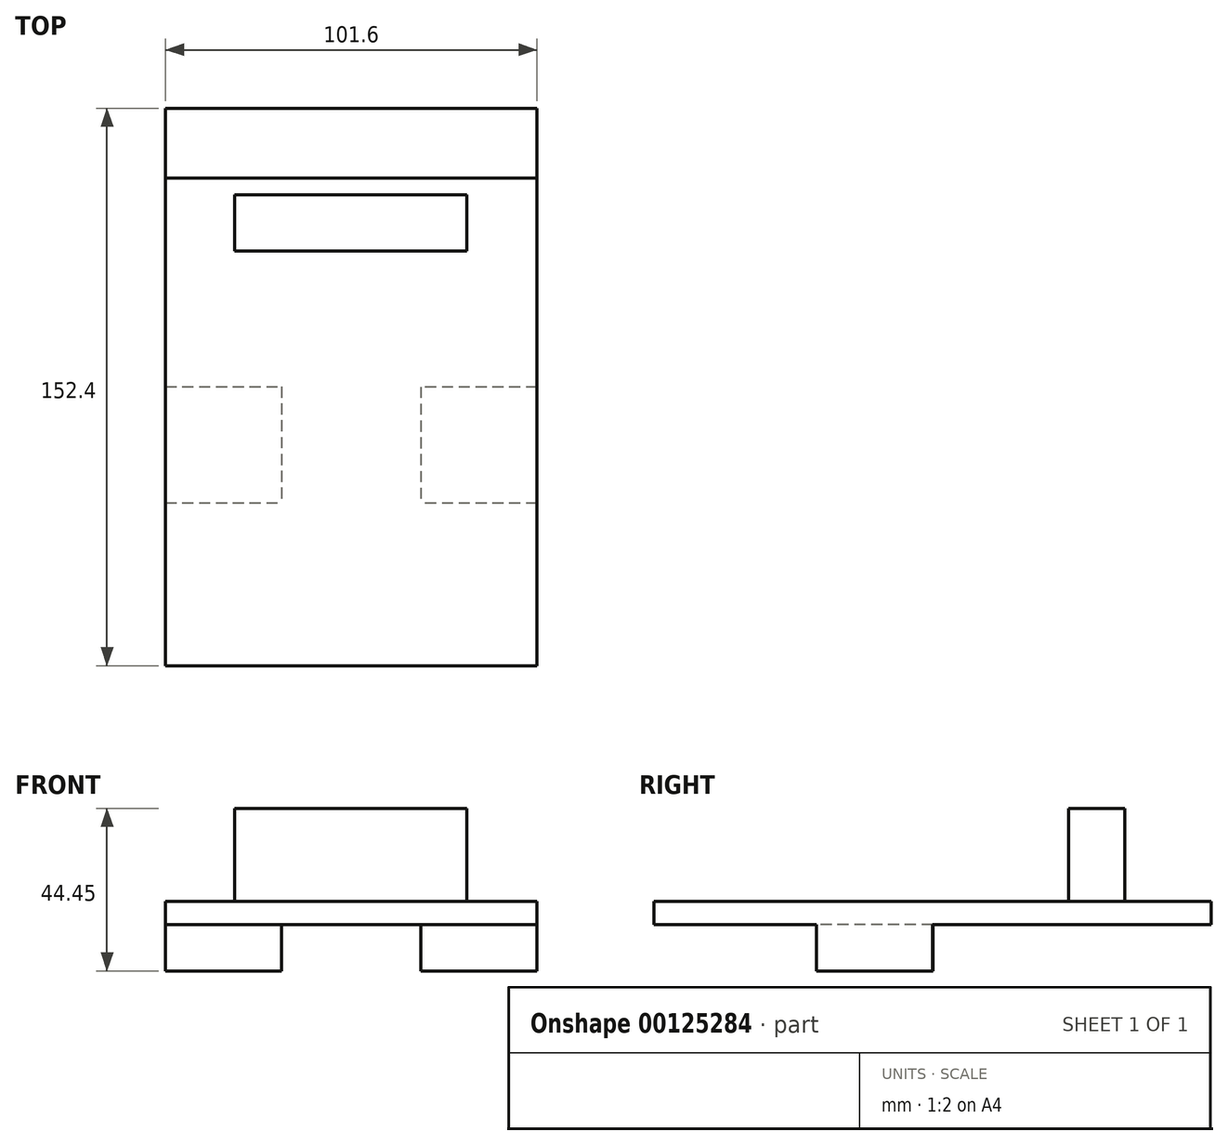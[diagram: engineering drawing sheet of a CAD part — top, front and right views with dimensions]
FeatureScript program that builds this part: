
annotation { "Feature Type Name" : "Feature", "Feature Type Description" : "" }
export const myFeature = defineFeature(function(context is Context, id is Id, definition is map)
    precondition{}
    {
        {
            var Q0;
            Q0=qCreatedBy(makeId("Top.planeOp"),FACE);
            var sketch = newSketch(context, id + "F0", { "sketchPlane" : qUnion([Q0])});
            skLineSegment(sketch, "E0.bottom", {"start": v(0, 0) * mm, "end": v(101.6, 0) * mm});
            skLineSegment(sketch, "E0.top", {"start": v(0, 152.4) * mm, "end": v(101.6, 152.4) * mm});
            skLineSegment(sketch, "E0.left", {"start": v(0, 0) * mm, "end": v(0, 152.4) * mm});
            skLineSegment(sketch, "E0.right", {"start": v(101.6, 0) * mm, "end": v(101.6, 152.4) * mm});
            skSolve(sketch);
        }
        {
            var Q0;
            Q0=makeQuery(id+"F0.imprint","IMPRINT",FACE,{"disambiguationData":[TD([[makeQuery(id+"F0.imprint","IMPRINT",EDGE,{"derivedFrom":sQuery(id+"F0.wireOp",EDGE,"E0.bottom")}),1.0]])]});
            extrude(context, id + "F1", {"entities" : qUnion([Q0]), "depth" : 6.35 * mm});
        }
        {
            var Q0;
            Q0=makeQuery(id+"F1.opExtrude","CAP_FACE",FACE,{"disambiguationData":[OSD([sQuery(id+"F0.wireOp",EDGE,"E0.bottom"),sQuery(id+"F0.wireOp",EDGE,"E0.top"),sQuery(id+"F0.wireOp",EDGE,"E0.left"),sQuery(id+"F0.wireOp",EDGE,"E0.right")])],"isStart":false});
            var sketch = newSketch(context, id + "F2", { "sketchPlane" : qUnion([Q0])});
            skLineSegment(sketch, "E1.bottom", {"start": v(18.86, 128.7) * mm, "end": v(82.36, 128.7) * mm});
            skLineSegment(sketch, "E1.top", {"start": v(18.86, 113.35) * mm, "end": v(82.36, 113.35) * mm});
            skLineSegment(sketch, "E1.left", {"start": v(18.86, 128.7) * mm, "end": v(18.86, 113.35) * mm});
            skLineSegment(sketch, "E1.right", {"start": v(82.36, 128.7) * mm, "end": v(82.36, 113.35) * mm});
            skSolve(sketch);
        }
        {
            var Q0;
            Q0=makeQuery(id+"F2.imprint","IMPRINT",FACE,{"disambiguationData":[TD([[makeQuery(id+"F2.imprint","IMPRINT",EDGE,{"derivedFrom":sQuery(id+"F2.wireOp",EDGE,"E1.bottom")}),-1.0]])]});
            extrude(context, id + "F3", {"entities" : qUnion([Q0]), "operationType" : NewBodyOperationType.ADD, "depth" : 25.4 * mm});
        }
        {
            var Q0;
            Q0=makeQuery(id+"F1.opExtrude","CAP_FACE",FACE,{"disambiguationData":[OSD([sQuery(id+"F0.wireOp",EDGE,"E0.bottom"),sQuery(id+"F0.wireOp",EDGE,"E0.top"),sQuery(id+"F0.wireOp",EDGE,"E0.left"),sQuery(id+"F0.wireOp",EDGE,"E0.right")])],"isStart":false});
            var sketch = newSketch(context, id + "F4", { "sketchPlane" : qUnion([Q0])});
            skLineSegment(sketch, "E2.bottom", {"start": v(0, 152.4) * mm, "end": v(101.6, 152.4) * mm});
            skLineSegment(sketch, "E2.top", {"start": v(0, 133.35) * mm, "end": v(101.6, 133.35) * mm});
            skLineSegment(sketch, "E2.left", {"start": v(0, 152.4) * mm, "end": v(0, 133.35) * mm});
            skLineSegment(sketch, "E2.right", {"start": v(101.6, 152.4) * mm, "end": v(101.6, 133.35) * mm});
            skSolve(sketch);
        }
        {
            var Q0;
            Q0=makeQuery(id+"F4.imprint","IMPRINT",FACE,{"disambiguationData":[TD([[makeQuery(id+"F4.imprint","IMPRINT",EDGE,{"derivedFrom":sQuery(id+"F4.wireOp",EDGE,"E2.bottom")}),-1.0]])]});
            extrude(context, id + "F5", {"entities" : qUnion([Q0]), "operationType" : NewBodyOperationType.ADD, "depth" : 5 / 812.8 * mm});
        }
        {
            var Q0;
            Q0=makeQuery(id+"F1.opExtrude","CAP_FACE",FACE,{"disambiguationData":[OSD([sQuery(id+"F0.wireOp",EDGE,"E0.bottom"),sQuery(id+"F0.wireOp",EDGE,"E0.top"),sQuery(id+"F0.wireOp",EDGE,"E0.left"),sQuery(id+"F0.wireOp",EDGE,"E0.right")])],"isStart":true});
            var sketch = newSketch(context, id + "F6", { "sketchPlane" : qUnion([Q0])});
            skLineSegment(sketch, "E3.bottom", {"start": v(0, -76.27) * mm, "end": v(31.75, -76.27) * mm});
            skLineSegment(sketch, "E3.top", {"start": v(0, -44.52) * mm, "end": v(31.75, -44.52) * mm});
            skLineSegment(sketch, "E3.left", {"start": v(0, -76.27) * mm, "end": v(0, -44.52) * mm});
            skLineSegment(sketch, "E3.right", {"start": v(31.75, -76.27) * mm, "end": v(31.75, -44.52) * mm});
            skSolve(sketch);
        }
        {
            var Q0;
            Q0=makeQuery(id+"F6.imprint","IMPRINT",FACE,{"disambiguationData":[TD([[makeQuery(id+"F6.imprint","IMPRINT",EDGE,{"derivedFrom":sQuery(id+"F6.wireOp",EDGE,"E3.bottom")}),1.0]])]});
            extrude(context, id + "F7", {"entities" : qUnion([Q0]), "operationType" : NewBodyOperationType.ADD, "depth" : 12.7 * mm});
        }
        {
            var Q0;
            Q0=makeQuery(id+"F1.opExtrude","CAP_FACE",FACE,{"disambiguationData":[OSD([sQuery(id+"F0.wireOp",EDGE,"E0.bottom"),sQuery(id+"F0.wireOp",EDGE,"E0.top"),sQuery(id+"F0.wireOp",EDGE,"E0.left"),sQuery(id+"F0.wireOp",EDGE,"E0.right")])],"isStart":true});
            var sketch = newSketch(context, id + "F8", { "sketchPlane" : qUnion([Q0])});
            skLineSegment(sketch, "E4.bottom", {"start": v(101.6, -76.2) * mm, "end": v(69.85, -76.2) * mm});
            skLineSegment(sketch, "E4.top", {"start": v(101.6, -44.45) * mm, "end": v(69.85, -44.45) * mm});
            skLineSegment(sketch, "E4.left", {"start": v(101.6, -76.2) * mm, "end": v(101.6, -44.45) * mm});
            skLineSegment(sketch, "E4.right", {"start": v(69.85, -76.2) * mm, "end": v(69.85, -44.45) * mm});
            skSolve(sketch);
        }
        {
            var Q0;
            Q0=makeQuery(id+"F8.imprint","IMPRINT",FACE,{"disambiguationData":[TD([[makeQuery(id+"F8.imprint","IMPRINT",EDGE,{"derivedFrom":sQuery(id+"F8.wireOp",EDGE,"E4.bottom")}),-1.0]])]});
            extrude(context, id + "F9", {"entities" : qUnion([Q0]), "operationType" : NewBodyOperationType.ADD, "depth" : 12.7 * mm});
        }
    });
